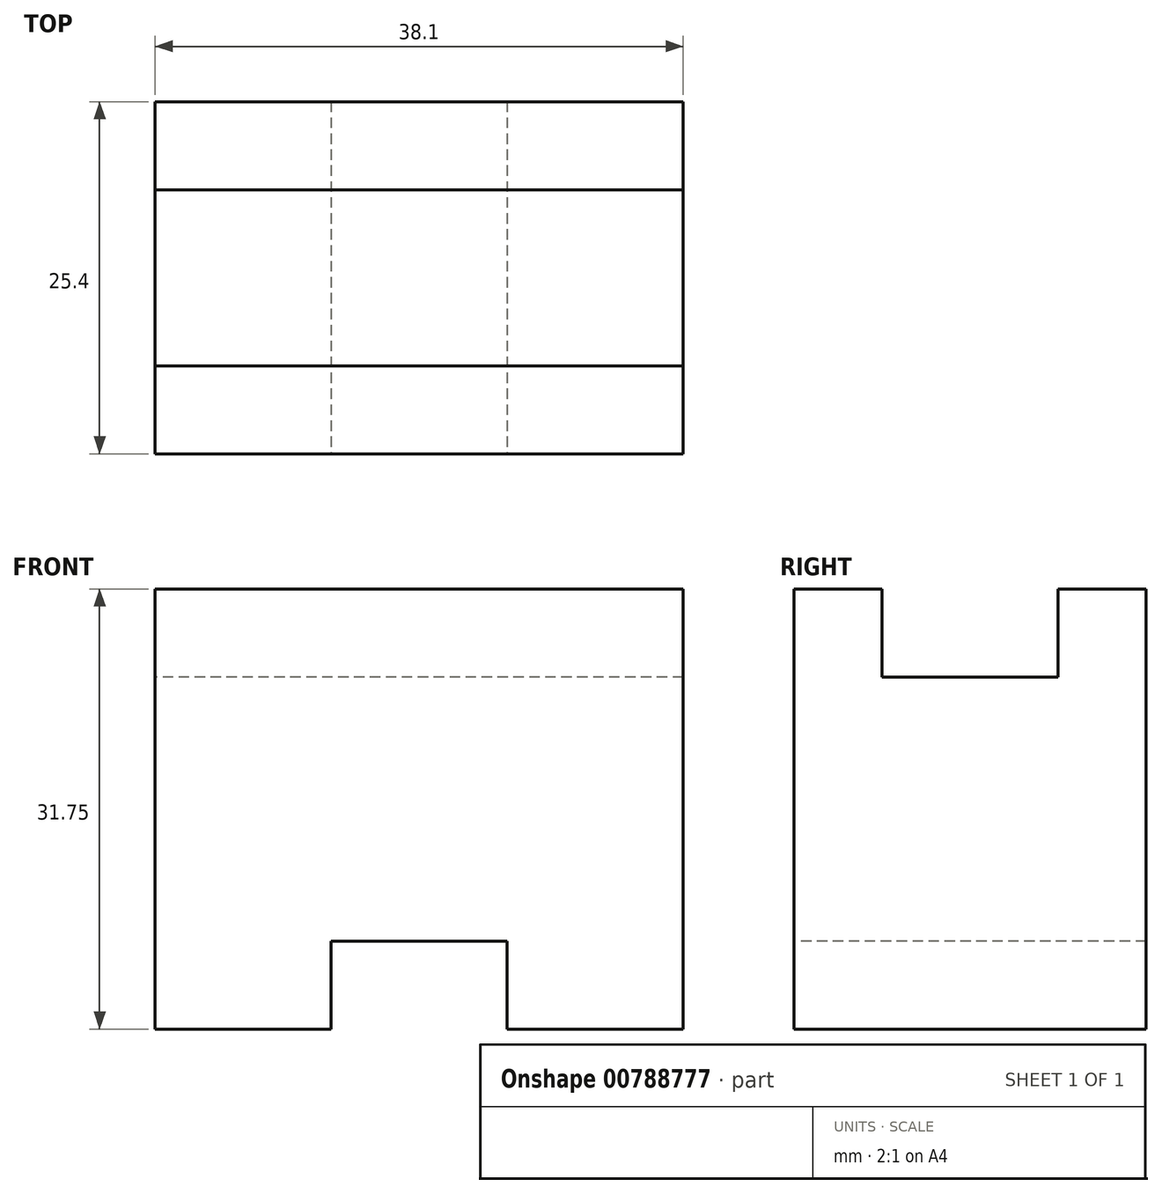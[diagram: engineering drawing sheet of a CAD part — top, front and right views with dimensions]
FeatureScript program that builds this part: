
annotation { "Feature Type Name" : "Feature", "Feature Type Description" : "" }
export const myFeature = defineFeature(function(context is Context, id is Id, definition is map)
    precondition{}
    {
        {
            var Q0;
            Q0=qCreatedBy(makeId("Right.planeOp"),FACE);
            var sketch = newSketch(context, id + "F0", { "sketchPlane" : qUnion([Q0])});
            skLineSegment(sketch, "E0", {"start": v(0, 0) * mm, "end": v(25.4, 0) * mm});
            skLineSegment(sketch, "E1", {"start": v(0, 0) * mm, "end": v(0, 31.75) * mm});
            skLineSegment(sketch, "E2", {"start": v(0, 31.75) * mm, "end": v(6.35, 31.75) * mm});
            skLineSegment(sketch, "E3", {"start": v(6.35, 31.75) * mm, "end": v(6.35, 25.4) * mm});
            skLineSegment(sketch, "E4", {"start": v(6.35, 25.4) * mm, "end": v(19.05, 25.4) * mm});
            skLineSegment(sketch, "E5", {"start": v(19.05, 25.4) * mm, "end": v(19.05, 31.75) * mm});
            skLineSegment(sketch, "E6", {"start": v(19.05, 31.75) * mm, "end": v(25.4, 31.75) * mm});
            skLineSegment(sketch, "E7", {"start": v(25.4, 31.75) * mm, "end": v(25.4, 0) * mm});
            skSolve(sketch);
        }
        {
            var Q0;
            Q0 = qSketchRegion(id + "F0", true);
            extrude(context, id + "F1", {"entities" : qUnion([Q0]), "depth" : 38.1 * mm, "offsetDistance" : 25.4 * mm});
        }
        {
            var Q0;
            Q0=makeQuery(id+"F1.opExtrude","SWEPT_FACE",FACE,{"disambiguationData":[OSD([sQuery(id+"F0.wireOp",EDGE,"E1")])]});
            var sketch = newSketch(context, id + "F2", { "sketchPlane" : qUnion([Q0])});
            skLineSegment(sketch, "E8", {"start": v(12.7, 0) * mm, "end": v(12.7, 6.35) * mm});
            skLineSegment(sketch, "E9", {"start": v(12.7, 6.35) * mm, "end": v(25.4, 6.35) * mm});
            skLineSegment(sketch, "E10", {"start": v(25.4, 6.35) * mm, "end": v(25.4, 0) * mm});
            skSolve(sketch);
        }
        {
            var Q0;
            {var subQ0=sQuery(id+"F2.wireOp",EDGE,"E8");Q0=makeQuery(id+"F2.imprint","IMPRINT",FACE,{"disambiguationData":[TD([[makeQuery(id+"F2.imprint","IMPRINT",EDGE,{"derivedFrom":subQ0}),-1.0]])]});}
            extrude(context, id + "F3", {"entities" : qUnion([Q0]), "operationType" : NewBodyOperationType.REMOVE, "endBound" : BoundingType.THROUGH_ALL, "oppositeDirection" : true, "depth" : 25.4 * mm, "offsetDistance" : 25.4 * mm});
        }
    });
